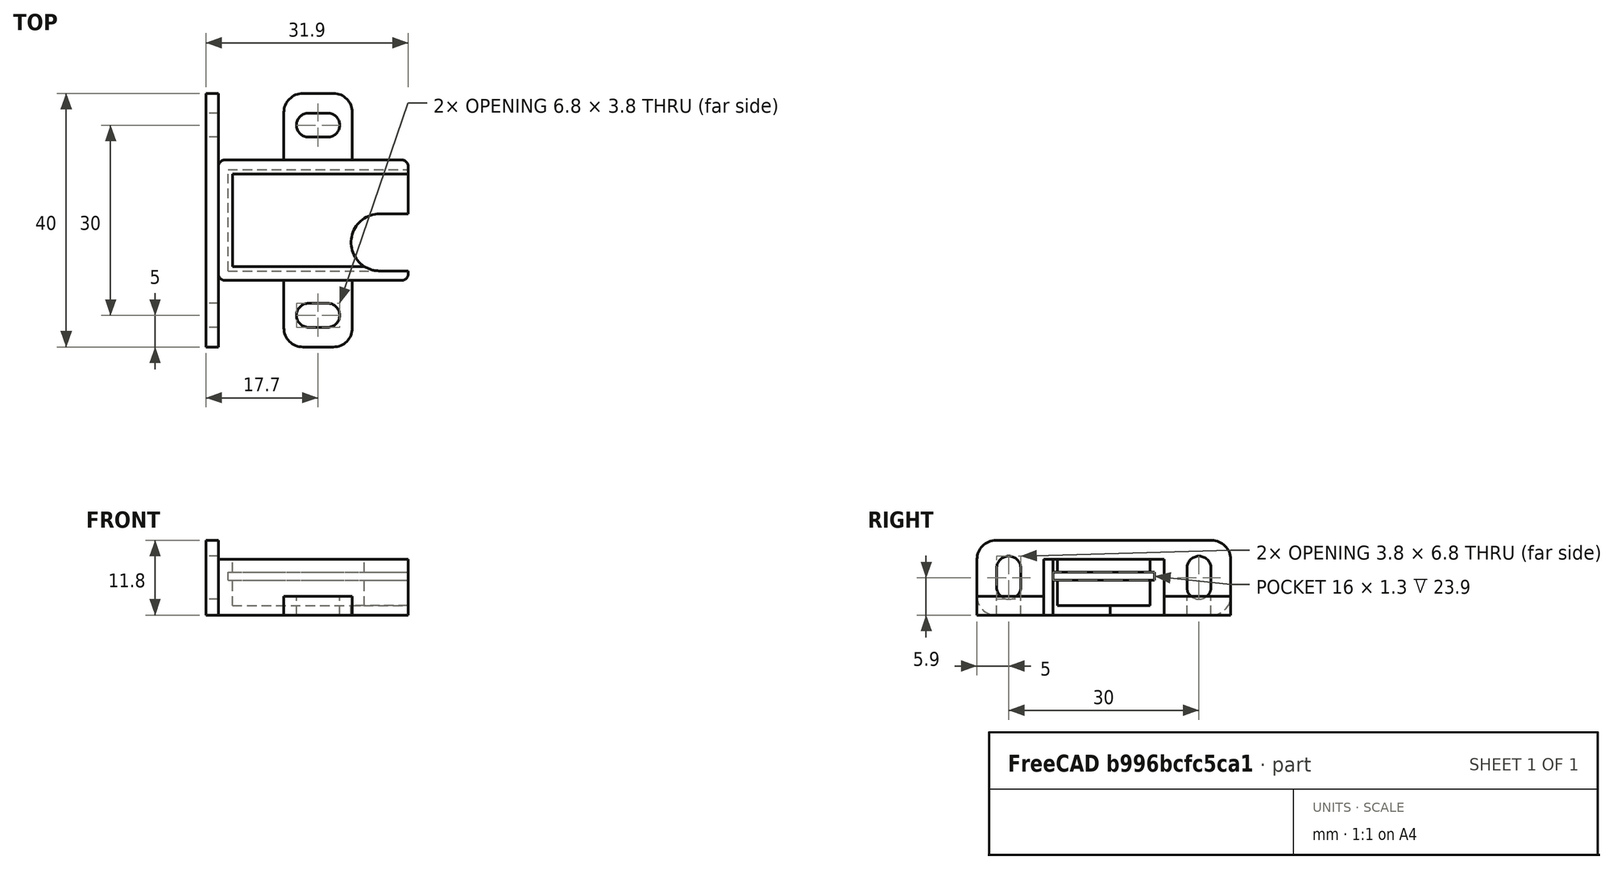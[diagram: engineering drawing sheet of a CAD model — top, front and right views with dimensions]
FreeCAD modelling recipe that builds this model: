
FCSTD DOCUMENT  (FreeCAD 0.19R)
Label: nrf24l01
License: FreeArt
LicenseURL: http://artlibre.org/licence/lal
objects: Part::Box×4, Part::Feature×2, Part::MultiFuse×2, Spreadsheet::Sheet×1, Part::Fillet×1, Part::Cylinder×1, Part::Cut×1, App::Part×1
note: 11 computed .brp shape members not serialized (recipe doc carries the construction recipe); baked Part::Feature solids carry a one-line shape summary decoded from their .brp

FEATURE [Spreadsheet::Sheet] Spreadsheet  label="p"
  cells = A1=pcb_x; B1(pcb_x)==28.4mm; A2=pcb_y; B2(pcb_y)==16mm; A3=pcb_z; B3(pcb_z)==1.3mm; A4=pcb_under; B4(pcb_under)==4mm; A5=side_wall; B5(side_wall)==1.5mm; A6=pcb_side_lane; B6(pcb_side_lane)==0.7mm; A7=bottom_wall; B7(bottom_wall)==1.5mm; A8=pcb_above; B8(pcb_above)==2mm; A9=antenna_r; B9(antenna_r)==4.5mm
FEATURE [Part::Box] Box  label="external cube"
  AttacherType = Attacher::AttachEngine3D
  Height = 8.8
  Length = 29.9
  Width = 19
  expr: Height = <<p>>.bottom_wall + <<p>>.pcb_under + <<p>>.pcb_z + <<p>>.pcb_above
  expr: Width = <<p>>.pcb_y + 2 * <<p>>.side_wall
  expr: Length = <<p>>.pcb_x + <<p>>.side_wall
FEATURE [Part::Box] Box006  label="internal cube"
  AttacherType = Attacher::AttachEngine3D
  Height = 7.3
  Length = 28.5
  Placement = pos=(2.2,2.2,1.5) rot=(0,0,1;0rad)
  Width = 14.6
  expr: .Placement.Base.y = <<p>>.side_wall + <<p>>.pcb_side_lane
  expr: .Placement.Base.x = <<p>>.side_wall + <<p>>.pcb_side_lane
  expr: .Placement.Base.z = <<p>>.bottom_wall
  expr: Height = <<p>>.pcb_under + <<p>>.pcb_z + <<p>>.pcb_above
  expr: Width = <<p>>.pcb_y - 2 * <<p>>.pcb_side_lane
  expr: Length = <<p>>.pcb_x - 2 * <<p>>.pcb_side_lane + <<p>>.side_wall
FEATURE [Part::Box] Box007  label="pcb extract cube"
  AttacherType = Attacher::AttachEngine3D
  Height = 1.3
  Length = 28.4
  Placement = pos=(1.5,1.5,5.5) rot=(0,0,1;0rad)
  Width = 16
  expr: .Placement.Base.y = <<p>>.side_wall
  expr: .Placement.Base.x = <<p>>.side_wall
  expr: Length = <<p>>.pcb_x
  expr: Width = <<p>>.pcb_y
  expr: .Placement.Base.z = <<p>>.bottom_wall + <<p>>.pcb_under
  expr: Height = <<p>>.pcb_z
FEATURE [Part::Fillet] Fillet  label="external fillet"
  Base = -> Box
  Edges = 4 edges r=1: [Edge1,Edge3,Edge5,Edge7]
FEATURE [Part::Feature] Cut002001  label="attach plane y dir001"
  shape: bbox 10.8 x 40 x 3 mm, 18 faces (baked)
FEATURE [Part::MultiFuse] Fusion001  label="solid fusion"
  Shapes = -> [Fillet,Cut002001]
FEATURE [Part::Cylinder] Cylinder  label="antenna hole"
  Angle = 360
  AttacherType = Attacher::AttachEngine3D
  Height = 10
  Placement = pos=(25.4,6,0) rot=(0,0,1;0rad)
  Radius = 4.5
  expr: .Placement.Base.x = <<p>>.side_wall + <<p>>.pcb_x - Radius
  expr: .Placement.Base.y = <<p>>.side_wall + Radius
  expr: Radius = <<p>>.antenna_r
FEATURE [Part::Box] Box008  label="antenna cube hole"
  AttacherType = Attacher::AttachEngine3D
  Height = 10
  Length = 4.5
  Placement = pos=(25.4,1.5,0) rot=(0,0,1;0rad)
  Width = 9
  expr: Width = 2 * <<p>>.antenna_r
  expr: Length = <<p>>.antenna_r
  expr: .Placement.Base.x = <<p>>.side_wall + <<p>>.pcb_x - Length
  expr: .Placement.Base.y = <<p>>.side_wall
FEATURE [Part::MultiFuse] Fusion  label="extract fusion"
  Shapes = -> [Box006,Box007,Cylinder,Box008]
FEATURE [Part::Cut] Cut  label="nrf24l01 cut"
  Base = -> Fusion001
  Tool = -> Fusion
FEATURE [App::Part] Part  label="nrf24l01 pcb box part"
  Group = -> [Box,Fillet,Fusion001,Fusion,Box007,Box006,Cut]
  Origin = -> Origin
FEATURE [Part::Feature] Body001001  label="attach plane y rotated dir001"
  Placement = pos=(0,-10.5,0) rot=(0,-1,0;1.5708rad)
  shape: bbox 2 x 40 x 11.8 mm, 20 faces (baked)
